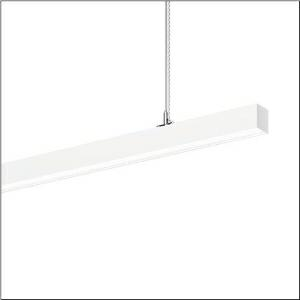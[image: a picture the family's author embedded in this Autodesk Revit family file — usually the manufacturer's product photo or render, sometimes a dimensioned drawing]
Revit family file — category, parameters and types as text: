
# Revit family: silica_r__21_51mx30tbt5w_3ed0
name_source: partatom
category: Lighting Fixtures
units: mm (PartAtom-declared; Revit-internal decimal feet)

## family parameters
Cut with Voids When Loaded = No
Host = Face
Light Source = No
Part Type = Normal
Room Calculation Point = No
Round Connector Dimension = Use Diameter
Shared = No

## types (1)
- --- (1 x LED, 5150 lm, 42.2 W, 6500K)
    Apparent Load = 42 VA
    CIE Flux Codes = 47 79 96 58 100
    Color Rendering = 80
    Color Temperature = 6500K
    Default Elevation = 1800 mm
    Description = Silica® 21, office luminaire, primary optical cover: cover, of PMMA, opal, light emission: direct/indirect distribution, primary light characteristic: symmetric, installation type: suspended mounting, LED, rated luminous flux: 5.150lm, luminous efficacy: 116lm/W, light colour: 8tw, colour temperature: 2700..6500K, control gear: ECG DALI, with terminal, 3+2-pole, max. 2.5mm², mains connection: 220..240V, AC, 50/60Hz, rated input power: 44.3W, luminaire housing, of aluminium, traffic white (RAL 9016), length: 1.504mm, width: 53mm, height: 53mm, protection rating (complete): IP20, insulation class (complete): insulation class I (protective earthing), certification: CE, permissible operating ambient temperature: 0..+35°C, standard: EN 50419, packaging unit: 1 piece
    Height = 53 mm
    Lamp = 1 x LED
    Lamp Light Flux = 5150 lm
    Lamp Power = 42.2 W
    Lamp count = 1
    Length = 1504 mm
    Luminous efficacy = 122 lm/W
    Manufacturer = Siteco
    ModVariant = No
    Model = 51MX30TBT5W
    Mounting Place = Ceiling
    Mounting Type = Pendant
    Number of Poles = 1
    OnlyDefault = Yes
    Power Factor = 1
    Product Name = Silica® 21
    Product group = office luminaire | ceiling pendant
    ProductGroupID = 905
    Protection Class = Protection class I
    Protection Degree = IP 20
    RLX_Detail_Level = 1
    RlxData = <blob elided: 18185 chars, md5=8e849ba5>
    Socket = socket
    Standby Power = 0 W
    System Light Flux = 5150 lm
    System Power = 42 W
    Type Comments = individual setting
    Type Image = l_1251642.jpg
    URL = http://relux.com
    VarID = @adj_045741
    Voltage = 0 V
    Weight = 0.00 kg
    Width = 53 mm

## geometry (parser evidence)
native form markers: Blend x4, Sweep x12
no freeform markers — native parametric forms only
